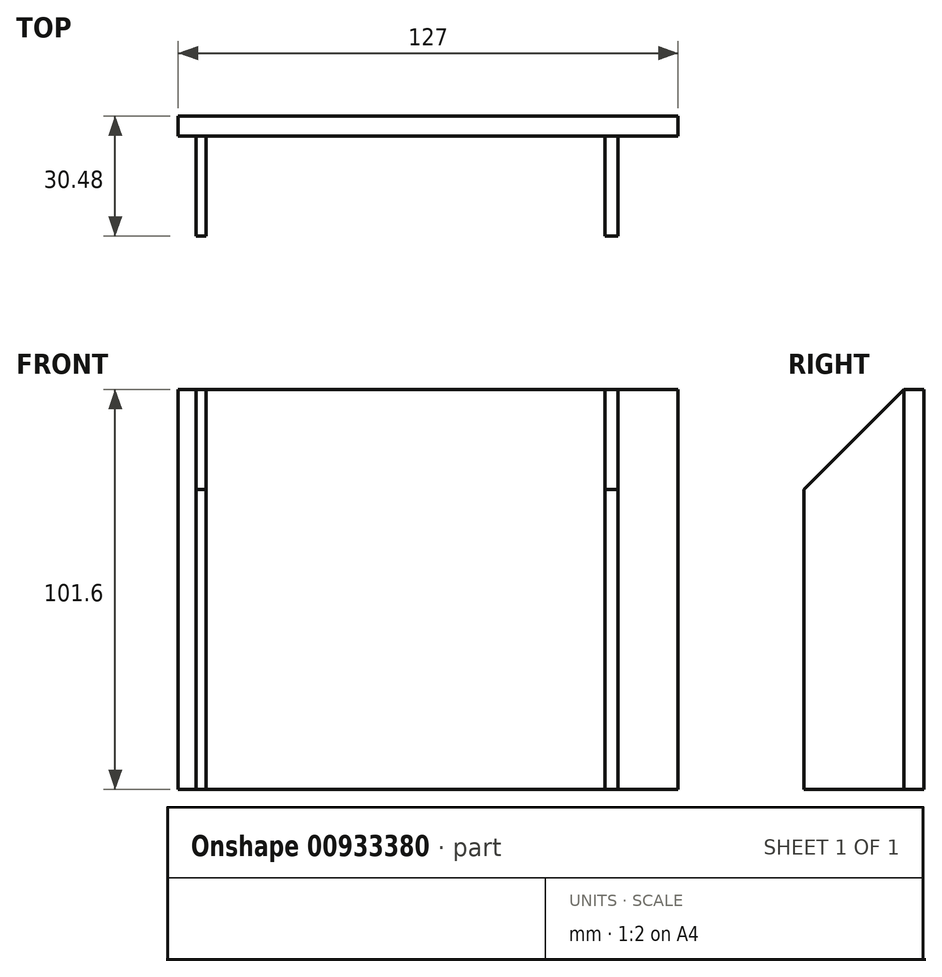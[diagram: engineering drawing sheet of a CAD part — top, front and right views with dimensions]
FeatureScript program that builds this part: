
annotation { "Feature Type Name" : "Feature", "Feature Type Description" : "" }
export const myFeature = defineFeature(function(context is Context, id is Id, definition is map)
    precondition{}
    {
        {
            var Q0;
            Q0=qCreatedBy(makeId("Top.planeOp"),FACE);
            var sketch = newSketch(context, id + "F0", { "sketchPlane" : qUnion([Q0])});
            skLineSegment(sketch, "E0.bottom", {"start": v(-62.5, 3.77) * mm, "end": v(64.5, 3.77) * mm});
            skLineSegment(sketch, "E0.top", {"start": v(-62.5, 8.85) * mm, "end": v(64.5, 8.85) * mm});
            skLineSegment(sketch, "E0.left", {"start": v(-62.5, 3.77) * mm, "end": v(-62.5, 8.85) * mm});
            skLineSegment(sketch, "E0.right", {"start": v(64.5, 3.77) * mm, "end": v(64.5, 8.85) * mm});
            skLineSegment(sketch, "E1.bottom", {"start": v(-57.97, 3.77) * mm, "end": v(-55.38, 3.77) * mm});
            skLineSegment(sketch, "E2.bottom", {"start": v(45.87, 3.77) * mm, "end": v(49.19, 3.77) * mm});
            skLineSegment(sketch, "E3.left", {"start": v(-57.97, 3.77) * mm, "end": v(-57.97, 3.77) * mm});
            skLineSegment(sketch, "E3.right", {"start": v(-55.38, 3.77) * mm, "end": v(-55.38, 3.77) * mm});
            skLineSegment(sketch, "E4.top", {"start": v(-57.97, -21.63) * mm, "end": v(-55.38, -21.63) * mm});
            skLineSegment(sketch, "E4.left", {"start": v(-57.97, 3.77) * mm, "end": v(-57.97, -21.63) * mm});
            skLineSegment(sketch, "E4.right", {"start": v(-55.38, 3.77) * mm, "end": v(-55.38, -21.63) * mm});
            skLineSegment(sketch, "E5.bottom", {"start": v(49.19, 3.77) * mm, "end": v(45.87, 3.77) * mm});
            skLineSegment(sketch, "E5.top", {"start": v(49.19, -21.63) * mm, "end": v(45.87, -21.63) * mm});
            skLineSegment(sketch, "E5.left", {"start": v(49.19, 3.77) * mm, "end": v(49.19, -21.63) * mm});
            skLineSegment(sketch, "E5.right", {"start": v(45.87, 3.77) * mm, "end": v(45.87, -21.63) * mm});
            skSolve(sketch);
        }
        {
            var Q0;
            Q0=makeQuery(id+"F0.imprint","IMPRINT",FACE,{"disambiguationData":[TD([[makeQuery(id+"F0.imprint","IMPRINT",EDGE,{"derivedFrom":sQuery(id+"F0.wireOp",EDGE,"E0.top")}),-1.0]])]});
            var Q1;
            Q1=makeQuery(id+"F0.imprint","IMPRINT",FACE,{"disambiguationData":[TD([[makeQuery(id+"F0.imprint","IMPRINT",EDGE,{"derivedFrom":sQuery(id+"F0.wireOp",EDGE,"E1.bottom")}),-1.0]])]});
            var Q2;
            Q2=makeQuery(id+"F0.imprint","IMPRINT",FACE,{"disambiguationData":[TD([[makeQuery(id+"F0.imprint","IMPRINT",EDGE,{"derivedFrom":sQuery(id+"F0.wireOp",EDGE,"E2.bottom")}),-1.0]])]});
            var Q3;
            Q3=makeQuery(id+"F0.imprint","IMPRINT",FACE,{"disambiguationData":[TD([[makeQuery(id+"F0.imprint","IMPRINT",EDGE,{"derivedFrom":sQuery(id+"F0.wireOp",EDGE,"E4.top")}),1.0]])]});
            var Q4;
            Q4=makeQuery(id+"F0.imprint","IMPRINT",FACE,{"disambiguationData":[TD([[makeQuery(id+"F0.imprint","IMPRINT",EDGE,{"derivedFrom":sQuery(id+"F0.wireOp",EDGE,"E5.top")}),-1.0]])]});
            extrude(context, id + "F1", {"entities" : qUnion([Q0, Q1, Q2, Q3, Q4]), "depth" : 101.6 * mm, "offsetDistance" : 25.4 * mm});
        }
        {
            var Q0;
            Q0=makeQuery(id+"F1.opExtrude","CAP_EDGE",EDGE,{"disambiguationData":[OSD([sQuery(id+"F0.wireOp",EDGE,"E4.top")])],"isStart":false});
            var Q1;
            Q1=makeQuery(id+"F1.opExtrude","CAP_EDGE",EDGE,{"disambiguationData":[OSD([sQuery(id+"F0.wireOp",EDGE,"E5.top")])],"isStart":false});
            chamfer(context, id + "F2", {"entities" : qUnion([Q0, Q1]), "width" : 25.4 * mm, "tangentPropagation" : true});
        }
    });
